# Revit family: Windows-Casement-Duratherm-Out_Swing-Wood
name_source: partatom
category: Windows
revit_build: Autodesk Revit 2017 (Build: 20190508_0315(x64)
units: mm (PartAtom-declared; Revit-internal decimal feet)

## family parameters
Always vertical = Yes
Cut with Voids When Loaded = No
Host = Wall
OmniClass Number = 23.30.20.00
OmniClass Title = Windows
Room Calculation Point = No
Shared = No

## types (2) — shared parameters
2D Width = 24"
2D Width Screen = 20 1/2"
Actual width = 24"
Analytic Construction = <None>
Assembly Code = B2020130
Default Sill Height = 31 1/2"
Edition number = 1
Glazing = Low E
Glazing Material = Glass ‐ Duratherm ‐ Solarban 60
Heat Transfer Coefficient (U) = 1.8738 W/(m²·K)
Height = 36"
Manufacturer = Duratherm Window Corporation
Maximum Recommended Height = 84"
Maximum Recommended Width = 36"
Minimum Recommended Height = 18"
Minimum Recommended Width = 18"
Model = Outswing
Product Guid = 8590ac4f-cb90-4974-b169-3745be2d4198
Product data url = https://bimobject.com
Rough Height = 37"
Rough Width = 25"
Size Restrictions = Sizes are available outside of the recommended maximum values, but please contact Duratherm to confirm availability
Solar Heat Gain Coefficient = 0.38
Thermal Resistance (R) = 0.5336 (m²·K)/W
Thickness = 6 1/2"
URL = http://www.durathermwindows.com
Visual Light Transmittance = 0.7
Wall Closure = By host
Width = 24"

## per-type parameters (varying)
| type | Description | Screen Required | Screen not Required |
| Custom Size with Screen | Outswing Window | Yes | No |
| Custom Size without Screen | Outswing Windows | No | Yes |

## geometry (parser evidence)
native form markers: Sweep x4
no freeform markers — native parametric forms only
